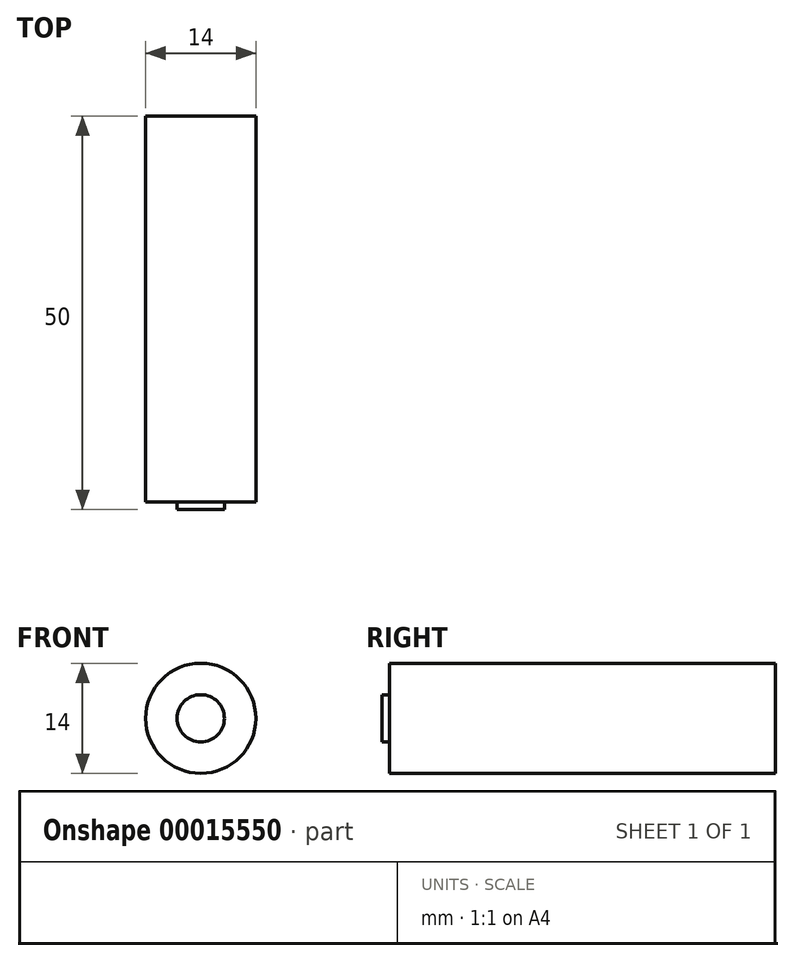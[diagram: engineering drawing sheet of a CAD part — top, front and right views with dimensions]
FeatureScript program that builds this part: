
annotation { "Feature Type Name" : "Feature", "Feature Type Description" : "" }
export const myFeature = defineFeature(function(context is Context, id is Id, definition is map)
    precondition{}
    {
        {
            var Q0;
            Q0=qCreatedBy(makeId("Front.planeOp"),FACE);
            var sketch = newSketch(context, id + "F0", { "sketchPlane" : qUnion([Q0])});
            skCircle(sketch, "E0", {"center": v(0, 0) * mm, "radius": 7 * mm});
            skSolve(sketch);
        }
        {
            var Q0;
            Q0 = qSketchRegion(id + "F0", true);
            extrude(context, id + "F1", {"entities" : qUnion([Q0]), "depth" : 49 * mm});
        }
        {
            var Q0;
            Q0=makeQuery(id+"F1.opExtrude","CAP_FACE",FACE,{"disambiguationData":[OSD([sQuery(id+"F0.wireOp",EDGE,"E0")])],"isStart":false});
            var sketch = newSketch(context, id + "F2", { "sketchPlane" : qUnion([Q0])});
            skCircle(sketch, "E1", {"center": v(0, 0) * mm, "radius": 3 * mm});
            skSolve(sketch);
        }
        {
            var Q0;
            Q0 = qSketchRegion(id + "F2", true);
            extrude(context, id + "F3", {"entities" : qUnion([Q0]), "operationType" : NewBodyOperationType.ADD, "depth" : 1 * mm});
        }
    });
